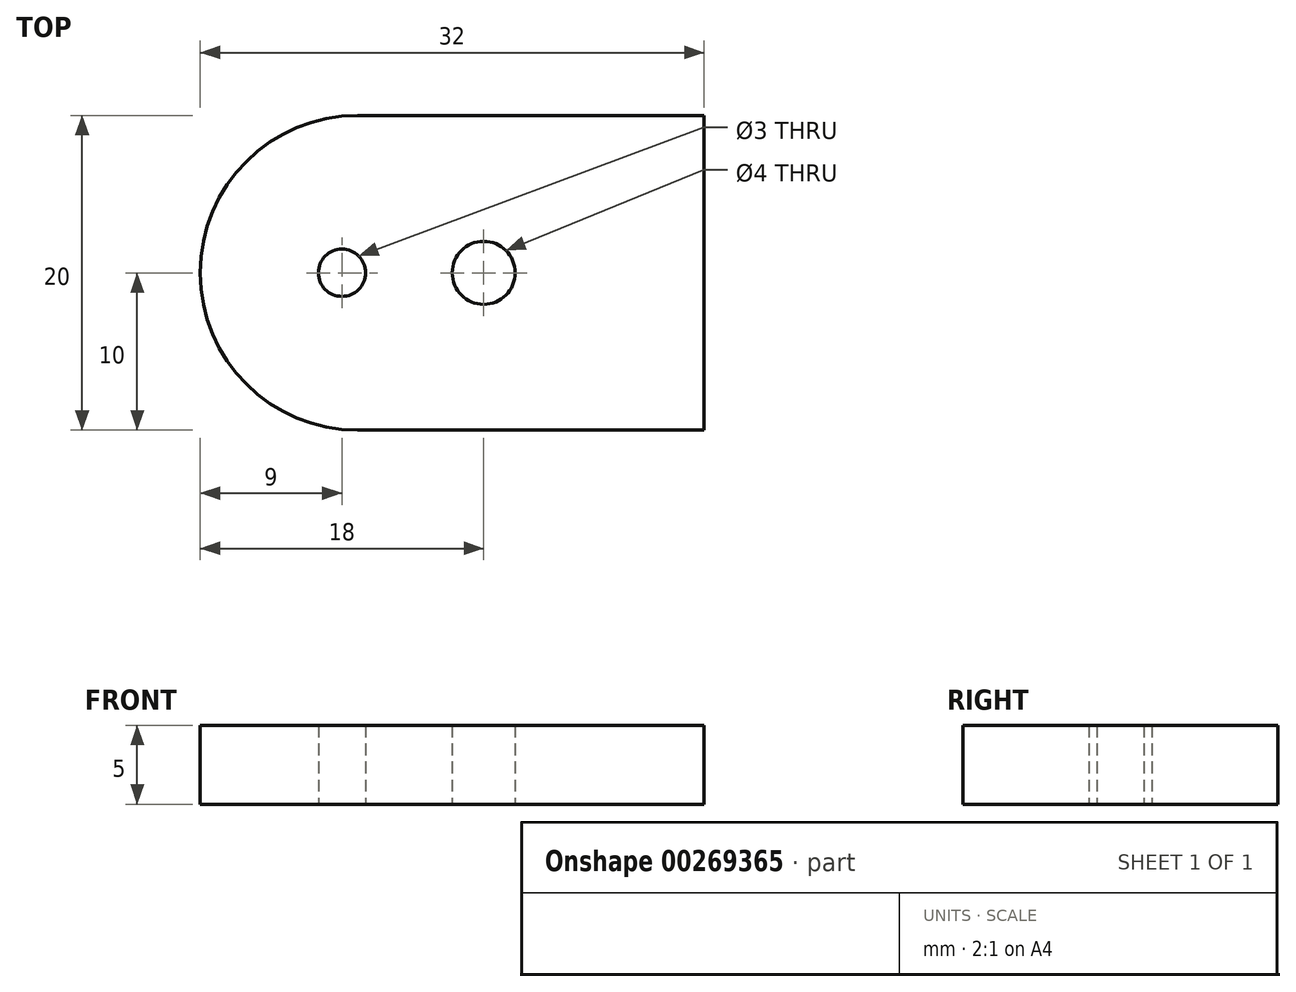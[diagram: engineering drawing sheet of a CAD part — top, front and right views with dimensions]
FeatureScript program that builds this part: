
annotation { "Feature Type Name" : "Feature", "Feature Type Description" : "" }
export const myFeature = defineFeature(function(context is Context, id is Id, definition is map)
    precondition{}
    {
        {
            var Q0;
            Q0=qCreatedBy(makeId("Top.planeOp"),FACE);
            var sketch = newSketch(context, id + "F0", { "sketchPlane" : qUnion([Q0])});
            skLineSegment(sketch, "E0.bottom", {"start": v(-6, 10) * mm, "end": v(16, 10) * mm});
            skLineSegment(sketch, "E0.top", {"start": v(-6, -10) * mm, "end": v(16, -10) * mm});
            skLineSegment(sketch, "E0.left", {"start": v(-16, 0) * mm, "end": v(-16, 0) * mm});
            skLineSegment(sketch, "E0.right", {"start": v(16, 10) * mm, "end": v(16, -10) * mm});
            skPoint(sketch, "E0.middle", {"position": v(0, 0) * mm});
            skLineSegment(sketch, "E1", {"start": v(0, 0) * mm, "end": v(2, 0) * mm});
            skCircle(sketch, "E2", {"center": v(2, 0) * mm, "radius": 2 * mm});
            skPoint(sketch, "E3.visualSharp", {"position": v(-16, 10) * mm});
            skArc(sketch, "E3.filletArc", {"start": v(-6, 10) * mm, "mid": v(-13.07, 7.07) * mm, "end": v(-16, 0) * mm});
            skPoint(sketch, "E4.visualSharp", {"position": v(-16, -10) * mm});
            skArc(sketch, "E4.filletArc", {"start": v(-16, 0) * mm, "mid": v(-13.07, -7.07) * mm, "end": v(-6, -10) * mm});
            skLineSegment(sketch, "E5", {"start": v(0, 0) * mm, "end": v(-7, 0) * mm});
            skCircle(sketch, "E6", {"center": v(-7, 0) * mm, "radius": 1.5 * mm});
            skSolve(sketch);
        }
        {
            var Q0;
            Q0 = qSketchRegion(id + "F0", true);
            extrude(context, id + "F1", {"entities" : qUnion([Q0]), "depth" : 5 * mm});
        }
    });
